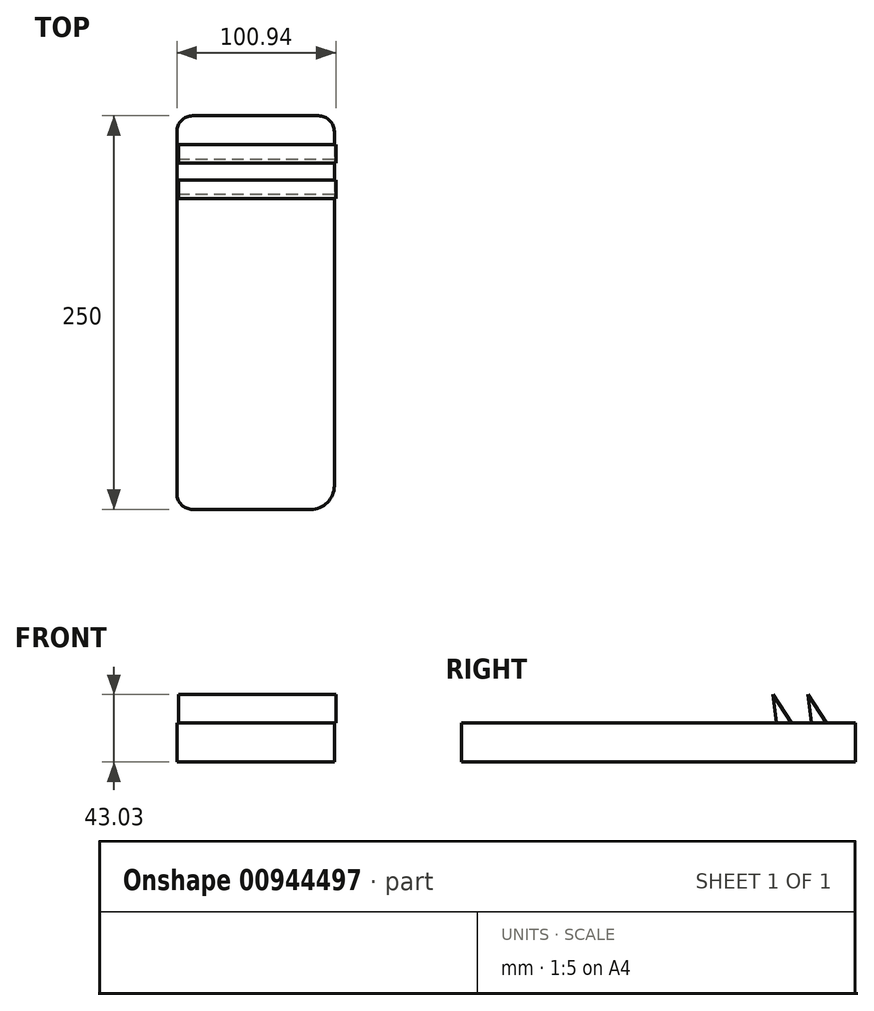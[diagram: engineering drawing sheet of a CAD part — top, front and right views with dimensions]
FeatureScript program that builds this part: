
annotation { "Feature Type Name" : "Feature", "Feature Type Description" : "" }
export const myFeature = defineFeature(function(context is Context, id is Id, definition is map)
    precondition{}
    {
        {
            var Q0;
            Q0=qCreatedBy(makeId("Right.planeOp"),FACE);
            var sketch = newSketch(context, id + "F0", { "sketchPlane" : qUnion([Q0])});
            skLineSegment(sketch, "E0", {"start": v(180.3, 25) * mm, "end": v(168.57, 43.03) * mm});
            skLineSegment(sketch, "E1", {"start": v(168.57, 43.03) * mm, "end": v(170.94, 25) * mm});
            skLineSegment(sketch, "E2", {"start": v(170.94, 25) * mm, "end": v(168.57, 43.03) * mm});
            skLineSegment(sketch, "E3", {"start": v(158, 25) * mm, "end": v(146.26, 43.03) * mm});
            skLineSegment(sketch, "E4", {"start": v(146.26, 43.03) * mm, "end": v(148.64, 25) * mm});
            skLineSegment(sketch, "E5", {"start": v(148.64, 25) * mm, "end": v(146.26, 43.03) * mm});
            skLineSegment(sketch, "E6", {"start": v(180.3, 25) * mm, "end": v(170.94, 25) * mm});
            skLineSegment(sketch, "E7", {"start": v(158, 25) * mm, "end": v(148.64, 25) * mm});
            skSolve(sketch);
        }
        {
            var Q0;
            Q0=qCreatedBy(makeId("Top.planeOp"),FACE);
            var sketch = newSketch(context, id + "F1", { "sketchPlane" : qUnion([Q0])});
            skLineSegment(sketch, "E8.bottom", {"start": v(-40.94, 198.69) * mm, "end": v(39.06, 198.69) * mm});
            skLineSegment(sketch, "E8.top", {"start": v(-40.94, -51.31) * mm, "end": v(34.06, -51.31) * mm});
            skLineSegment(sketch, "E8.left", {"start": v(-50.94, 188.69) * mm, "end": v(-50.94, -41.31) * mm});
            skLineSegment(sketch, "E8.right", {"start": v(49.06, 188.69) * mm, "end": v(49.06, -36.31) * mm});
            skPoint(sketch, "E9.visualSharp", {"position": v(-50.94, 198.69) * mm});
            skArc(sketch, "E9.filletArc", {"start": v(-40.94, 198.69) * mm, "mid": v(-48.02, 195.76) * mm, "end": v(-50.94, 188.69) * mm});
            skPoint(sketch, "E10.visualSharp", {"position": v(49.06, 198.69) * mm});
            skArc(sketch, "E10.filletArc", {"start": v(49.06, 188.69) * mm, "mid": v(46.13, 195.76) * mm, "end": v(39.06, 198.69) * mm});
            skPoint(sketch, "E11.visualSharp", {"position": v(49.06, -51.31) * mm});
            skArc(sketch, "E11.filletArc", {"start": v(34.06, -51.31) * mm, "mid": v(44.66, -46.92) * mm, "end": v(49.06, -36.31) * mm});
            skPoint(sketch, "E12.visualSharp", {"position": v(-50.94, -51.31) * mm});
            skArc(sketch, "E12.filletArc", {"start": v(-50.94, -41.31) * mm, "mid": v(-48.02, -48.38) * mm, "end": v(-40.94, -51.31) * mm});
            skSolve(sketch);
        }
        {
            var Q0;
            Q0 = qSketchRegion(id + "F1", true);
            extrude(context, id + "F2", {"entities" : qUnion([Q0]), "depth" : 25 * mm, "offsetDistance" : 25 * mm});
        }
        {
            var Q0;
            Q0 = qSketchRegion(id + "F0", true);
            extrude(context, id + "F3", {"entities" : qUnion([Q0]), "operationType" : NewBodyOperationType.ADD, "endBound" : BoundingType.SYMMETRIC, "depth" : 100 * mm, "offsetDistance" : 25 * mm});
        }
    });
